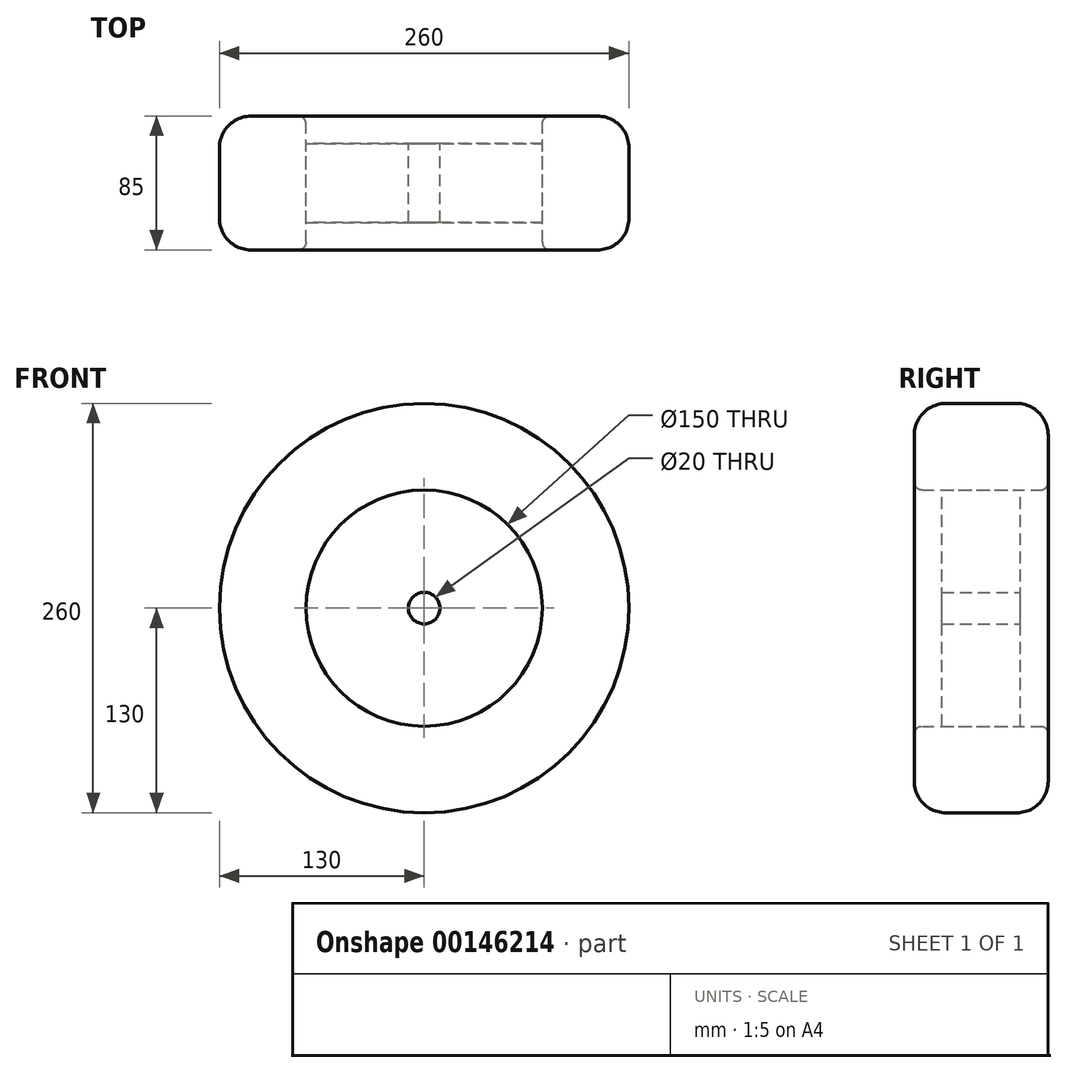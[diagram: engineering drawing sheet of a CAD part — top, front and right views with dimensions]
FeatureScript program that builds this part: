
annotation { "Feature Type Name" : "Feature", "Feature Type Description" : "" }
export const myFeature = defineFeature(function(context is Context, id is Id, definition is map)
    precondition{}
    {
        {
            var Q0;
            Q0=qCreatedBy(makeId("Front.planeOp"),FACE);
            var sketch = newSketch(context, id + "F0", { "sketchPlane" : qUnion([Q0])});
            skCircle(sketch, "E0", {"center": v(0, 0) * mm, "radius": 130 * mm});
            skCircle(sketch, "E1", {"center": v(0, 0) * mm, "radius": 75 * mm});
            skCircle(sketch, "E2", {"center": v(0, 0) * mm, "radius": 10 * mm});
            skSolve(sketch);
        }
        {
            var Q0;
            Q0=makeQuery(id+"F0.imprint","IMPRINT",FACE,{"disambiguationData":[TD([[makeQuery(id+"F0.imprint","IMPRINT",EDGE,{"derivedFrom":sQuery(id+"F0.wireOp",EDGE,"E1")}),1.0]])]});
            extrude(context, id + "F1", {"entities" : qUnion([Q0]), "depth" : 50 * mm, "symmetric" : true});
        }
        {
            var Q0;
            Q0 = qSketchRegion(id + "F0", true);
            extrude(context, id + "F2", {"entities" : qUnion([Q0]), "depth" : 85 * mm, "symmetric" : true});
        }
        {
            var Q0;
            Q0=makeQuery(id+"F2.opExtrude","CAP_EDGE",EDGE,{"disambiguationData":[OSD([sQuery(id+"F0.wireOp",EDGE,"E0")])],"isStart":false});
            var Q1;
            Q1=makeQuery(id+"F2.opExtrude","CAP_EDGE",EDGE,{"disambiguationData":[OSD([sQuery(id+"F0.wireOp",EDGE,"E0")])],"isStart":true});
            fillet(context, id + "F3", {"entities" : qUnion([Q0, Q1]), "radius" : 20 * mm, "tangentPropagation" : true, "allowEdgeOverflow" : false});
        }
        {
            var Q0;
            Q0=makeQuery(id+"F2.opExtrude","CAP_EDGE",EDGE,{"disambiguationData":[OSD([sQuery(id+"F0.wireOp",EDGE,"E1")])],"isStart":false});
            var Q1;
            Q1=makeQuery(id+"F2.opExtrude","CAP_EDGE",EDGE,{"disambiguationData":[OSD([sQuery(id+"F0.wireOp",EDGE,"E1")])],"isStart":true});
            fillet(context, id + "F4", {"entities" : qUnion([Q0, Q1]), "radius" : 5 * mm, "tangentPropagation" : true, "allowEdgeOverflow" : false});
        }
    });
